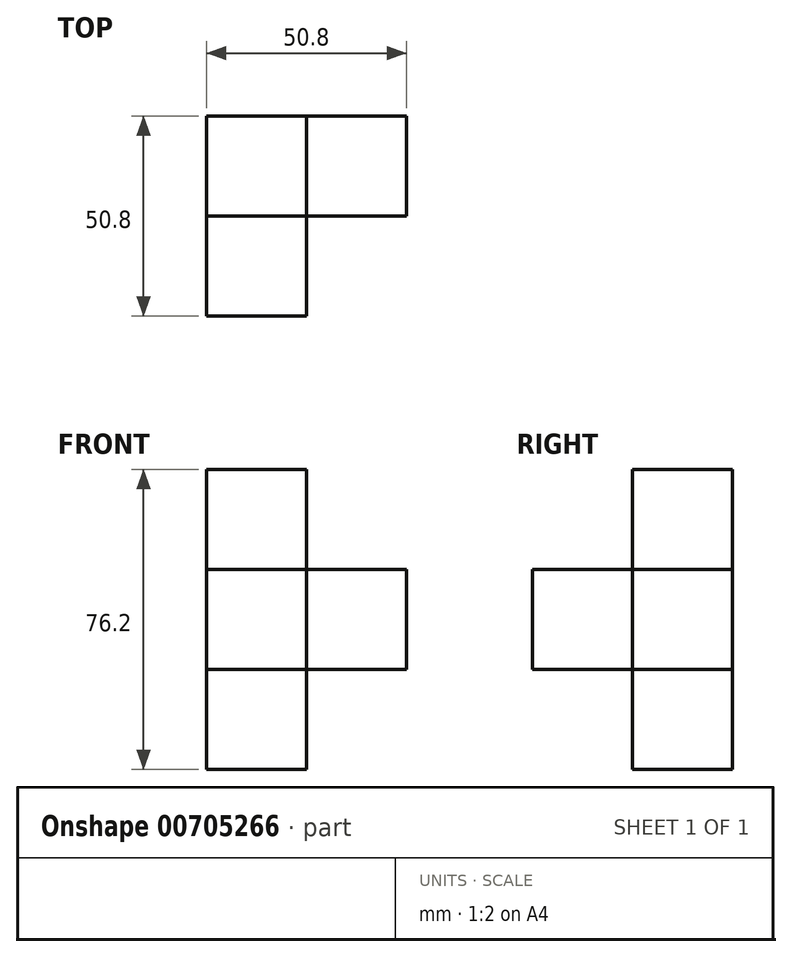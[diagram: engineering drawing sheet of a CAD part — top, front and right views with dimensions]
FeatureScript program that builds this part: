
annotation { "Feature Type Name" : "Feature", "Feature Type Description" : "" }
export const myFeature = defineFeature(function(context is Context, id is Id, definition is map)
    precondition{}
    {
        {
            var Q0;
            Q0=qCreatedBy(makeId("Right.planeOp"),FACE);
            var sketch = newSketch(context, id + "F0", { "sketchPlane" : qUnion([Q0])});
            skLineSegment(sketch, "E0.bottom", {"start": v(0, 0) * mm, "end": v(-25.4, 0) * mm});
            skLineSegment(sketch, "E0.top", {"start": v(0, 25.4) * mm, "end": v(-25.4, 25.4) * mm});
            skLineSegment(sketch, "E0.left", {"start": v(0, 0) * mm, "end": v(0, 25.4) * mm});
            skLineSegment(sketch, "E0.right", {"start": v(-25.4, 0) * mm, "end": v(-25.4, 25.4) * mm});
            skLineSegment(sketch, "E1.top", {"start": v(0, 50.8) * mm, "end": v(-25.4, 50.8) * mm});
            skLineSegment(sketch, "E1.left", {"start": v(0, 25.4) * mm, "end": v(0, 50.8) * mm});
            skLineSegment(sketch, "E1.right", {"start": v(-25.4, 25.4) * mm, "end": v(-25.4, 50.8) * mm});
            skLineSegment(sketch, "E2.top", {"start": v(0, -25.4) * mm, "end": v(-25.4, -25.4) * mm});
            skLineSegment(sketch, "E2.left", {"start": v(0, 0) * mm, "end": v(0, -25.4) * mm});
            skLineSegment(sketch, "E2.right", {"start": v(-25.4, 0) * mm, "end": v(-25.4, -25.4) * mm});
            skLineSegment(sketch, "E3.bottom", {"start": v(-25.4, 25.4) * mm, "end": v(-50.8, 25.4) * mm});
            skLineSegment(sketch, "E3.top", {"start": v(-25.4, 0) * mm, "end": v(-50.8, 0) * mm});
            skLineSegment(sketch, "E3.left", {"start": v(-25.4, 25.4) * mm, "end": v(-25.4, 0) * mm});
            skLineSegment(sketch, "E3.right", {"start": v(-50.8, 25.4) * mm, "end": v(-50.8, 0) * mm});
            skLineSegment(sketch, "E4.bottom", {"start": v(-50.8, 0) * mm, "end": v(-25.4, 0) * mm});
            skLineSegment(sketch, "E4.top", {"start": v(-50.8, -25.4) * mm, "end": v(-25.4, -25.4) * mm});
            skLineSegment(sketch, "E4.left", {"start": v(-50.8, 0) * mm, "end": v(-50.8, -25.4) * mm});
            skSolve(sketch);
        }
        {
            var Q0;
            Q0=makeQuery(id+"F0.imprint","IMPRINT",FACE,{"disambiguationData":[TD([[makeQuery(id+"F0.imprint","IMPRINT",EDGE,{"derivedFrom":sQuery(id+"F0.wireOp",EDGE,"E0.top")}),-1.0]])]});
            var Q1;
            Q1=makeQuery(id+"F0.imprint","IMPRINT",FACE,{"disambiguationData":[TD([[makeQuery(id+"F0.imprint","IMPRINT",EDGE,{"derivedFrom":sQuery(id+"F0.wireOp",EDGE,"E3.bottom")}),1.0]])]});
            var Q2;
            Q2=makeQuery(id+"F0.imprint","IMPRINT",FACE,{"disambiguationData":[TD([[makeQuery(id+"F0.imprint","IMPRINT",EDGE,{"derivedFrom":sQuery(id+"F0.wireOp",EDGE,"E4.bottom")}),-1.0]])]});
            var Q3;
            Q3=makeQuery(id+"F0.imprint","IMPRINT",FACE,{"disambiguationData":[TD([[makeQuery(id+"F0.imprint","IMPRINT",EDGE,{"derivedFrom":sQuery(id+"F0.wireOp",EDGE,"E0.bottom")}),1.0]])]});
            var Q4;
            Q4=makeQuery(id+"F0.imprint","IMPRINT",FACE,{"disambiguationData":[TD([[makeQuery(id+"F0.imprint","IMPRINT",EDGE,{"derivedFrom":sQuery(id+"F0.wireOp",EDGE,"E0.left")}),1.0]])]});
            extrude(context, id + "F1", {"entities" : qUnion([Q0, Q1, Q2, Q3, Q4]), "depth" : 25.4 * mm, "offsetDistance" : 25.4 * mm});
        }
        {
            var Q0;
            Q0=makeQuery(id+"F1.opExtrude","CAP_FACE",FACE,{"disambiguationData":[OSD([sQuery(id+"F0.wireOp",EDGE,"E0.left"),sQuery(id+"F0.wireOp",EDGE,"E1.top"),sQuery(id+"F0.wireOp",EDGE,"E1.left"),sQuery(id+"F0.wireOp",EDGE,"E1.right"),sQuery(id+"F0.wireOp",EDGE,"E2.top"),sQuery(id+"F0.wireOp",EDGE,"E2.left"),sQuery(id+"F0.wireOp",EDGE,"E3.bottom"),sQuery(id+"F0.wireOp",EDGE,"E3.right"),sQuery(id+"F0.wireOp",EDGE,"E4.top"),sQuery(id+"F0.wireOp",EDGE,"E4.left")])],"isStart":false});
            var sketch = newSketch(context, id + "F2", { "sketchPlane" : qUnion([Q0])});
            skLineSegment(sketch, "E5.bottom", {"start": v(-25.4, 25.4) * mm, "end": v(0, 25.4) * mm});
            skLineSegment(sketch, "E5.top", {"start": v(-25.4, 0) * mm, "end": v(0, 0) * mm});
            skLineSegment(sketch, "E5.left", {"start": v(-25.4, 25.4) * mm, "end": v(-25.4, 0) * mm});
            skLineSegment(sketch, "E5.right", {"start": v(0, 25.4) * mm, "end": v(0, 0) * mm});
            skSolve(sketch);
        }
        {
            var Q0;
            Q0=makeQuery(id+"F2.imprint","IMPRINT",FACE,{"disambiguationData":[TD([[makeQuery(id+"F2.imprint","IMPRINT",EDGE,{"derivedFrom":sQuery(id+"F2.wireOp",EDGE,"E5.bottom")}),-1.0]])]});
            extrude(context, id + "F3", {"entities" : qUnion([Q0]), "operationType" : NewBodyOperationType.ADD, "depth" : 25.4 * mm, "offsetDistance" : 25.4 * mm});
        }
    });
